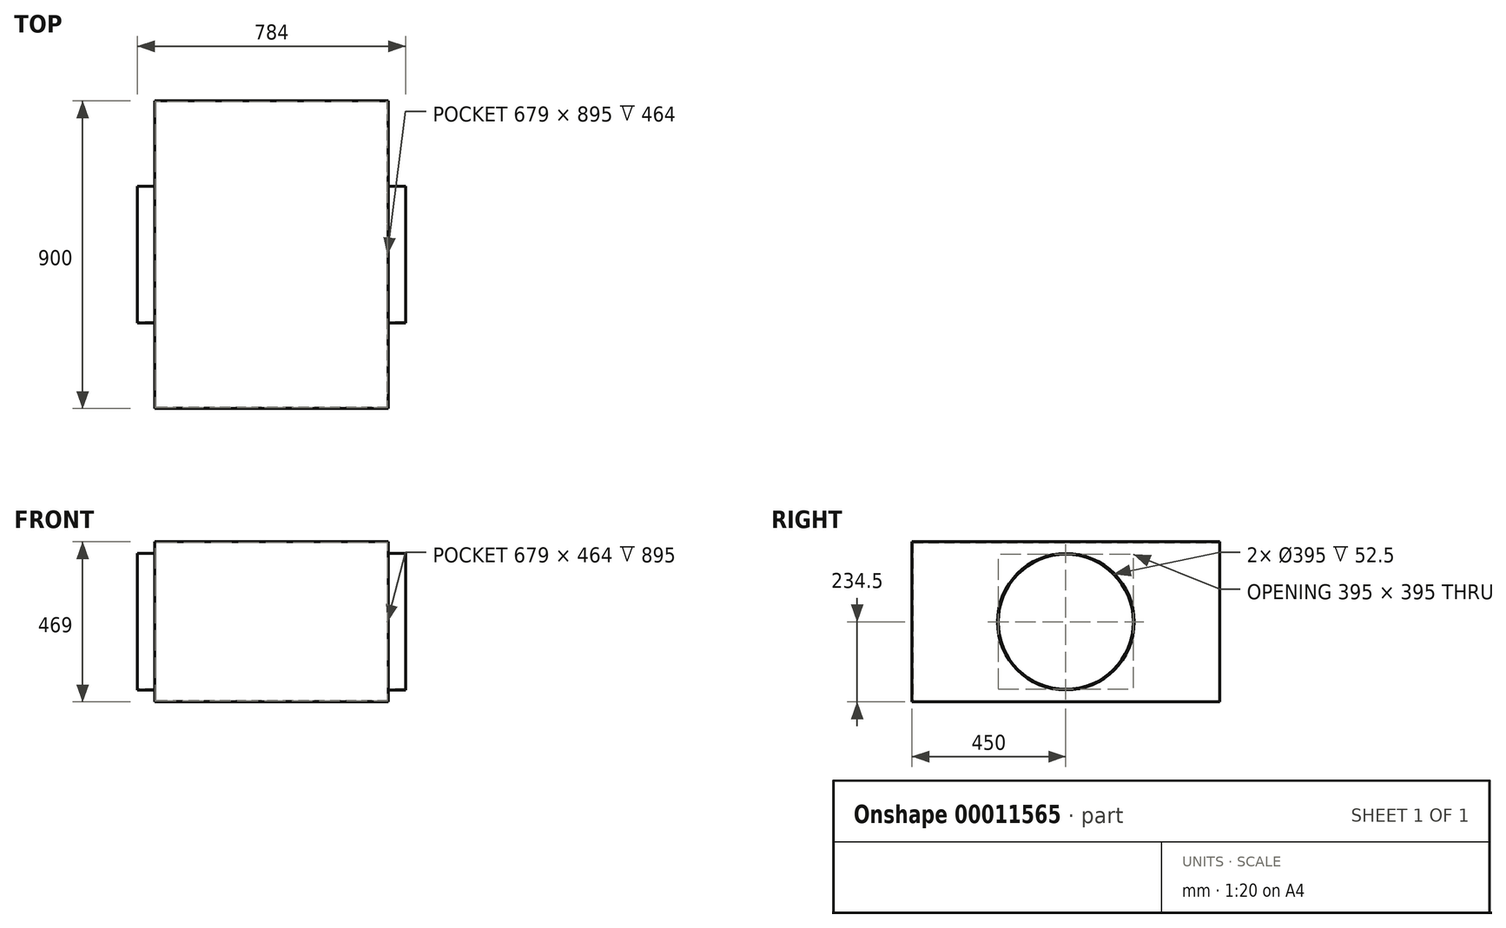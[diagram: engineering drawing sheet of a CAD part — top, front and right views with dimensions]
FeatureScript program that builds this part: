
annotation { "Feature Type Name" : "Feature", "Feature Type Description" : "" }
export const myFeature = defineFeature(function(context is Context, id is Id, definition is map)
    precondition{}
    {
        {
            var Q0;
            Q0=qCreatedBy(makeId("Top.planeOp"),FACE);
            var sketch = newSketch(context, id + "F0", { "sketchPlane" : qUnion([Q0])});
            skLineSegment(sketch, "E0.rect.bottom", {"start": v(342, -450) * mm, "end": v(-342, -450) * mm});
            skLineSegment(sketch, "E0.rect.top", {"start": v(342, 450) * mm, "end": v(-342, 450) * mm});
            skLineSegment(sketch, "E0.rect.left", {"start": v(342, -450) * mm, "end": v(342, 450) * mm});
            skLineSegment(sketch, "E0.rect.right", {"start": v(-342, -450) * mm, "end": v(-342, 450) * mm});
            skPoint(sketch, "E0.rect.middle", {"position": v(0, 0) * mm});
            skSolve(sketch);
        }
        {
            var Q0;
            Q0=makeQuery(id+"F0.imprint","IMPRINT",FACE,{"disambiguationData":[TD([[makeQuery(id+"F0.imprint","IMPRINT",EDGE,{"derivedFrom":sQuery(id+"F0.wireOp",EDGE,"E0.rect.bottom")}),-1.0]])]});
            extrude(context, id + "F1", {"entities" : qUnion([Q0]), "endBound" : BoundingType.SYMMETRIC, "depth" : 469 * mm});
        }
        {
            var Q0;
            Q0=qCreatedBy(makeId("Right.planeOp"),FACE);
            var sketch = newSketch(context, id + "F2", { "sketchPlane" : qUnion([Q0])});
            skCircle(sketch, "E1", {"center": v(0, 0) * mm, "radius": 200 * mm});
            skSolve(sketch);
        }
        {
            var Q0;
            Q0=qSketchRegion(id+"F2",true);
            extrude(context, id + "F3", {"entities" : qUnion([Q0]), "operationType" : NewBodyOperationType.ADD, "endBound" : BoundingType.SYMMETRIC, "depth" : 784 * mm});
        }
        {
            var Q0;
            Q0=makeQuery(id+"F3.opExtrude","CAP_FACE",FACE,{"disambiguationData":[OSD([sQuery(id+"F2.wireOp",EDGE,"E1")])],"isStart":false});
            var Q1;
            Q1=makeQuery(id+"F3.opExtrude","CAP_FACE",FACE,{"disambiguationData":[OSD([sQuery(id+"F2.wireOp",EDGE,"E1")])],"isStart":true});
            shell(context, id + "F4", {"entities" : qUnion([Q0, Q1]), "thickness" : 2.5 * mm});
        }
    });
